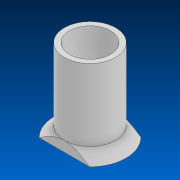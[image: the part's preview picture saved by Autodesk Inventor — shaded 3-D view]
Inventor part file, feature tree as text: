
AUTODESK INVENTOR PART (.ipt)
format: ipt  version: 2022.2 (Build 262287000, 287)  size: 111,616 bytes
history: native  units: in
note: dims shown in document units (in); Inventor stores cm internally (conversion verified against a paired STEP export)
features: sketch x2, revolve x1, extrude x1
ambient origin geometry x8: Origin, YZ Plane, XZ Plane, XY Plane, X Axis, Y Axis, Z Axis, Center Point
bodies: Solid1 (feature_tree)
feature tree (4):
  revolve  "Revolution1"  [1 undecoded]
  extrude  "Extrusion1"  TaperAngle=45.0deg  [1 undecoded]
  sketch  "Sketch2"  dims[d3=2.0in d4=0.5in]
  sketch  "Sketch3"  dims[d5=0.125in d6=45.0deg d7=0.25in d8=90.0deg d9=0.0in d10=0.0in]
note: 2 required parameter values undecoded (feature->parameter linkage not recoverable at this tier; creation-order binding heuristic only, values carry confidence <= 0.55)